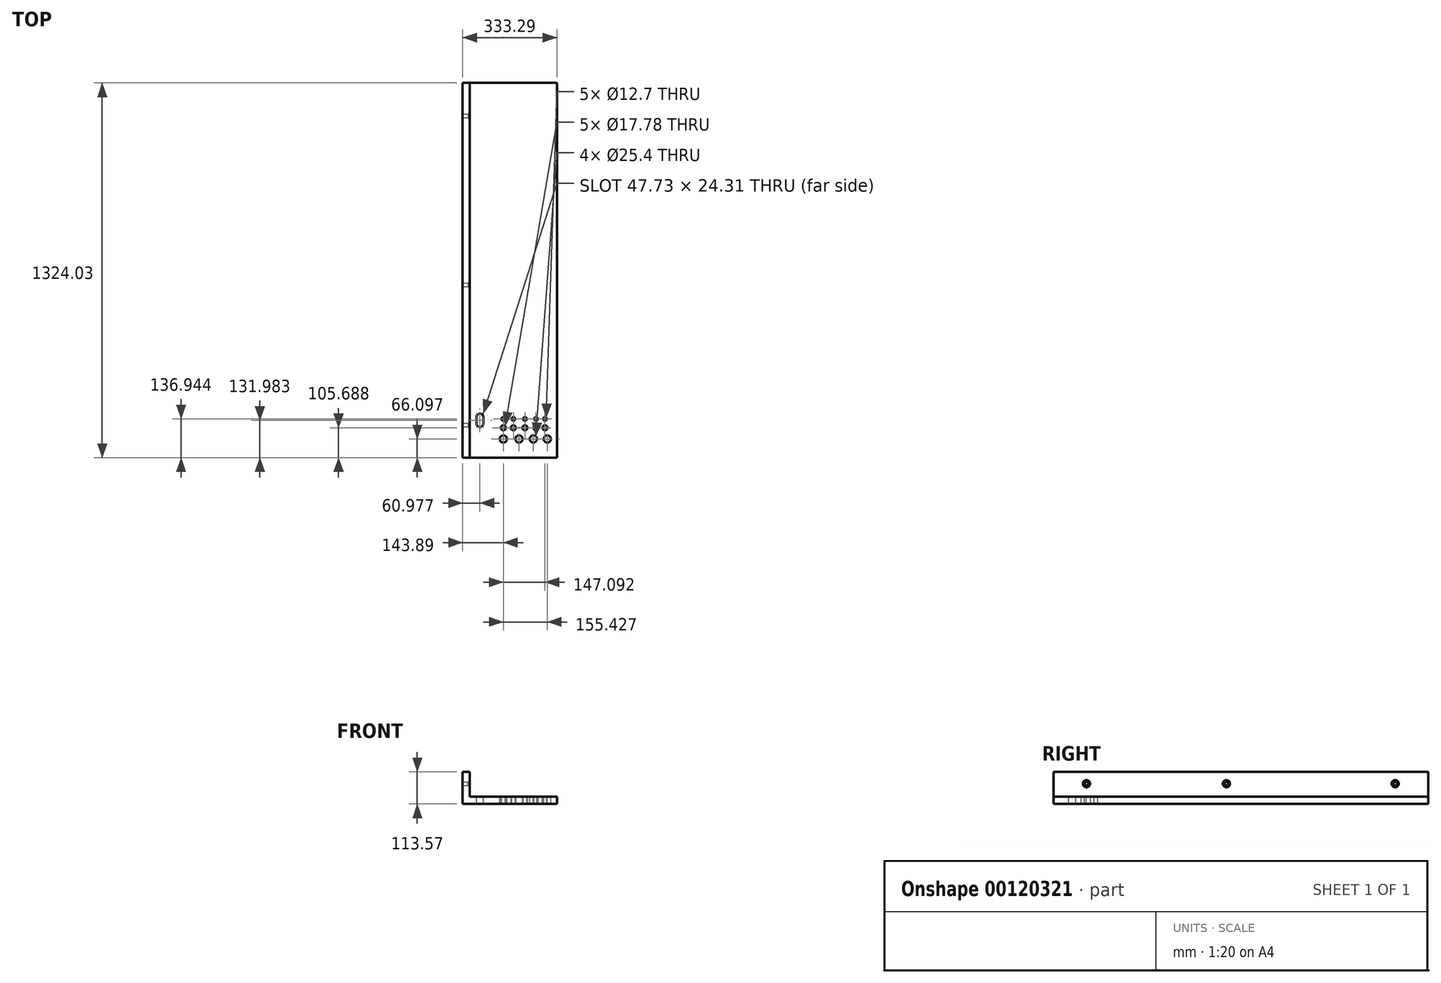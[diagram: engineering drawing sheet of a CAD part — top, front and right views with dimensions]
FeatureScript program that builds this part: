
annotation { "Feature Type Name" : "Feature", "Feature Type Description" : "" }
export const myFeature = defineFeature(function(context is Context, id is Id, definition is map)
    precondition{}
    {
        {
            var Q0;
            Q0=qCreatedBy(makeId("Top.planeOp"),FACE);
            var sketch = newSketch(context, id + "F0", { "sketchPlane" : qUnion([Q0])});
            skLineSegment(sketch, "E0.bottom", {"start": v(-154.05, 84.32) * mm, "end": v(153.84, 84.32) * mm});
            skLineSegment(sketch, "E0.top", {"start": v(-154.05, -115.94) * mm, "end": v(153.84, -115.94) * mm});
            skLineSegment(sketch, "E0.left", {"start": v(-154.05, 84.32) * mm, "end": v(-154.05, -115.94) * mm});
            skLineSegment(sketch, "E0.right", {"start": v(153.84, 84.32) * mm, "end": v(153.84, -115.94) * mm});
            skSolve(sketch);
        }
        {
            var Q0;
            Q0=makeQuery(id+"F0.imprint","IMPRINT",FACE,{"disambiguationData":[TD([[makeQuery(id+"F0.imprint","IMPRINT",EDGE,{"derivedFrom":sQuery(id+"F0.wireOp",EDGE,"E0.bottom")}),-1.0]])]});
            extrude(context, id + "F1", {"entities" : qUnion([Q0]), "depth" : 25.4 * mm});
        }
        {
            var Q0;
            Q0=makeQuery(id+"F1.opExtrude","SWEPT_FACE",FACE,{"disambiguationData":[OSD([sQuery(id+"F0.wireOp",EDGE,"E0.bottom")])]});
            var sketch = newSketch(context, id + "F2", { "sketchPlane" : qUnion([Q0])});
            skLineSegment(sketch, "E1.bottom", {"start": v(-153.84, 25.4) * mm, "end": v(154.05, 25.4) * mm});
            skLineSegment(sketch, "E1.top", {"start": v(-153.84, 0) * mm, "end": v(154.05, 0) * mm});
            skLineSegment(sketch, "E1.left", {"start": v(-153.84, 25.4) * mm, "end": v(-153.84, 0) * mm});
            skLineSegment(sketch, "E1.right", {"start": v(154.05, 25.4) * mm, "end": v(154.05, 0) * mm});
            skSolve(sketch);
        }
        {
            var Q0;
            Q0=makeQuery(id+"F2.imprint","IMPRINT",FACE,{"disambiguationData":[TD([[makeQuery(id+"F2.imprint","IMPRINT",EDGE,{"derivedFrom":sQuery(id+"F2.wireOp",EDGE,"E1.bottom")}),1.0]])]});
            extrude(context, id + "F3", {"entities" : qUnion([Q0]), "operationType" : NewBodyOperationType.ADD, "depth" : 174.76 * mm});
        }
        {
            var Q0;
            Q0=makeQuery(id+"F3.opExtrude","CAP_FACE",FACE,{"disambiguationData":[OSD([sQuery(id+"F2.wireOp",EDGE,"E1.bottom"),sQuery(id+"F2.wireOp",EDGE,"E1.top"),sQuery(id+"F2.wireOp",EDGE,"E1.left"),sQuery(id+"F2.wireOp",EDGE,"E1.right")])],"isStart":false});
            extrude(context, id + "F4", {"entities" : qUnion([Q0]), "operationType" : NewBodyOperationType.ADD, "depth" : 949 * mm});
        }
        {
            var Q0;
            {var subQ0=sQuery(id+"F2.wireOp",EDGE,"E1.right");Q0=makeQuery(id+"F4.boolean.opBoolean","MERGE",FACE,{"derivedFrom":[makeQuery(id+"F3.boolean.opBoolean","MERGE",FACE,{"derivedFrom":[makeQuery(id+"F1.opExtrude","SWEPT_FACE",FACE,{"disambiguationData":[OSD([sQuery(id+"F0.wireOp",EDGE,"E0.left")])]}),makeQuery(id+"F3.opExtrude","SWEPT_FACE",FACE,{"disambiguationData":[OSD([subQ0])]})]}),makeQuery(id+"F4.opExtrude","SWEPT_FACE",FACE,{"disambiguationData":[OSD([subQ0])]})]});}
            var sketch = newSketch(context, id + "F5", { "sketchPlane" : qUnion([Q0])});
            skLineSegment(sketch, "E2.bottom", {"start": v(-1208.09, 25.4) * mm, "end": v(115.94, 25.4) * mm});
            skLineSegment(sketch, "E2.top", {"start": v(-1208.09, 0) * mm, "end": v(115.94, 0) * mm});
            skLineSegment(sketch, "E2.left", {"start": v(-1208.09, 25.4) * mm, "end": v(-1208.09, 0) * mm});
            skLineSegment(sketch, "E2.right", {"start": v(115.94, 25.4) * mm, "end": v(115.94, 0) * mm});
            skSolve(sketch);
        }
        {
            var Q0;
            Q0=makeQuery(id+"F5.imprint","IMPRINT",FACE,{"disambiguationData":[TD([[makeQuery(id+"F5.imprint","IMPRINT",EDGE,{"derivedFrom":sQuery(id+"F5.wireOp",EDGE,"E2.bottom")}),-1.0]])]});
            extrude(context, id + "F6", {"entities" : qUnion([Q0]), "operationType" : NewBodyOperationType.ADD, "depth" : 25.4 * mm});
        }
        {
            var Q0;
            {var subQ0=sQuery(id+"F2.wireOp",EDGE,"E1.bottom");Q0=makeQuery(id+"F6.boolean.opBoolean","MERGE",FACE,{"derivedFrom":[makeQuery(id+"F4.boolean.opBoolean","MERGE",FACE,{"derivedFrom":[makeQuery(id+"F3.boolean.opBoolean","MERGE",FACE,{"derivedFrom":[makeQuery(id+"F1.opExtrude","CAP_FACE",FACE,{"disambiguationData":[OSD([sQuery(id+"F0.wireOp",EDGE,"E0.bottom"),sQuery(id+"F0.wireOp",EDGE,"E0.top"),sQuery(id+"F0.wireOp",EDGE,"E0.left"),sQuery(id+"F0.wireOp",EDGE,"E0.right")])],"isStart":false}),makeQuery(id+"F3.opExtrude","SWEPT_FACE",FACE,{"disambiguationData":[OSD([subQ0])]})]}),makeQuery(id+"F4.opExtrude","SWEPT_FACE",FACE,{"disambiguationData":[OSD([subQ0])]})]}),makeQuery(id+"F6.opExtrude","SWEPT_FACE",FACE,{"disambiguationData":[OSD([sQuery(id+"F5.wireOp",EDGE,"E2.bottom")])]})]});}
            var sketch = newSketch(context, id + "F7", { "sketchPlane" : qUnion([Q0])});
            skLineSegment(sketch, "E3.bottom", {"start": v(-179.45, -115.94) * mm, "end": v(-154.05, -115.94) * mm});
            skLineSegment(sketch, "E3.top", {"start": v(-179.45, 1208.09) * mm, "end": v(-154.05, 1208.09) * mm});
            skLineSegment(sketch, "E3.left", {"start": v(-179.45, -115.94) * mm, "end": v(-179.45, 1208.09) * mm});
            skLineSegment(sketch, "E3.right", {"start": v(-154.05, -115.94) * mm, "end": v(-154.05, 1208.09) * mm});
            skSolve(sketch);
        }
        {
            var Q0;
            Q0=makeQuery(id+"F7.imprint","IMPRINT",FACE,{"disambiguationData":[TD([[makeQuery(id+"F7.imprint","IMPRINT",EDGE,{"derivedFrom":sQuery(id+"F7.wireOp",EDGE,"E3.bottom")}),1.0]])]});
            extrude(context, id + "F8", {"entities" : qUnion([Q0]), "operationType" : NewBodyOperationType.ADD, "depth" : 88.17 * mm});
        }
        {
            var Q0;
            Q0=makeQuery(id+"F8.opExtrude","SWEPT_FACE",FACE,{"disambiguationData":[OSD([sQuery(id+"F7.wireOp",EDGE,"E3.right")])]});
            var sketch = newSketch(context, id + "F9", { "sketchPlane" : qUnion([Q0])});
            skPoint(sketch, "E4", {"position": v(0, 71.74) * mm});
            skPoint(sketch, "E5", {"position": v(1091.25, 71.74) * mm});
            skPoint(sketch, "E6", {"position": v(494.8, 71.74) * mm});
            skSolve(sketch);
        }
        {
            var Q0;
            Q0=sQuery(id+"F9.wireOp",VERTEX,"E4");
            var Q1;
            Q1=sQuery(id+"F9.wireOp",VERTEX,"E6");
            var Q2;
            Q2=sQuery(id+"F9.wireOp",VERTEX,"E5");
            var Q3;
            Q3=makeQuery(id+"F1.opExtrude","SWEPT_BODY",BODY,{"disambiguationData":[OSD([sQuery(id+"F0.wireOp",EDGE,"E0.bottom"),sQuery(id+"F0.wireOp",EDGE,"E0.top"),sQuery(id+"F0.wireOp",EDGE,"E0.left"),sQuery(id+"F0.wireOp",EDGE,"E0.right")])]});
            hole(context, id + "F10", {"style" : HoleStyle.C_SINK, "endStyle" : HoleEndStyle.THROUGH, "holeDiameter" : 12.7 * mm, "cSinkDiameter" : 25.4 * mm, "cSinkAngle" : 90 * degree, "locations" : qUnion([Q0, Q1, Q2]), "scope" : qUnion([Q3]), "isTappedThrough" : true});
        }
        {
            var Q0;
            {var subQ0=sQuery(id+"F2.wireOp",EDGE,"E1.bottom");Q0=makeQuery(id+"F6.boolean.opBoolean","MERGE",FACE,{"derivedFrom":[makeQuery(id+"F4.boolean.opBoolean","MERGE",FACE,{"derivedFrom":[makeQuery(id+"F3.boolean.opBoolean","MERGE",FACE,{"derivedFrom":[makeQuery(id+"F1.opExtrude","CAP_FACE",FACE,{"disambiguationData":[OSD([sQuery(id+"F0.wireOp",EDGE,"E0.bottom"),sQuery(id+"F0.wireOp",EDGE,"E0.top"),sQuery(id+"F0.wireOp",EDGE,"E0.left"),sQuery(id+"F0.wireOp",EDGE,"E0.right")])],"isStart":false}),makeQuery(id+"F3.opExtrude","SWEPT_FACE",FACE,{"disambiguationData":[OSD([subQ0])]})]}),makeQuery(id+"F4.opExtrude","SWEPT_FACE",FACE,{"disambiguationData":[OSD([subQ0])]})]}),makeQuery(id+"F6.opExtrude","SWEPT_FACE",FACE,{"disambiguationData":[OSD([sQuery(id+"F5.wireOp",EDGE,"E2.bottom")])]})]});}
            var sketch = newSketch(context, id + "F11", { "sketchPlane" : qUnion([Q0])});
            skLineSegment(sketch, "E7", {"start": v(-130.63, -43.56) * mm, "end": v(-130.63, -63.37) * mm});
            skLineSegment(sketch, "E8", {"start": v(-130.63, -63.37) * mm, "end": v(-130.63, -43.56) * mm});
            skLineSegment(sketch, "E9", {"start": v(-106.32, -43.56) * mm, "end": v(-106.32, -66.98) * mm});
            skArc(sketch, "E10", {"start": v(-106.32, -43.56) * mm, "mid": v(-118.47, -31.4) * mm, "end": v(-130.63, -43.56) * mm});
            skLineSegment(sketch, "E11", {"start": v(-130.63, -66.98) * mm, "end": v(-130.63, -63.37) * mm});
            skArc(sketch, "E12", {"start": v(-130.63, -66.98) * mm, "mid": v(-118.47, -79.13) * mm, "end": v(-106.32, -66.98) * mm});
            skLineSegment(sketch, "E13", {"start": v(-130.63, 4.33) * mm, "end": v(-130.63, 27.75) * mm});
            skLineSegment(sketch, "E14", {"start": v(-106.32, 4.33) * mm, "end": v(-106.32, 27.75) * mm});
            skArc(sketch, "E15", {"start": v(-106.32, 27.75) * mm, "mid": v(-118.47, 39.9) * mm, "end": v(-130.63, 27.75) * mm});
            skArc(sketch, "E16", {"start": v(-130.63, 4.33) * mm, "mid": v(-118.47, -7.82) * mm, "end": v(-106.32, 4.33) * mm});
            skCircle(sketch, "E17", {"center": v(-35.56, 21) * mm, "radius": 7.41 * mm});
            skCircle(sketch, "E18", {"center": v(-35.56, -10.25) * mm, "radius": 11.38 * mm});
            skCircle(sketch, "E19", {"center": v(-35.56, -49.84) * mm, "radius": 15.67 * mm});
            skCircle(sketch, "E20", {"center": v(0, 21) * mm, "radius": 7.5 * mm});
            skCircle(sketch, "E21", {"center": v(40.69, 21) * mm, "radius": 6.8 * mm});
            skCircle(sketch, "E22", {"center": v(79.76, 21) * mm, "radius": 8.62 * mm});
            skCircle(sketch, "E23", {"center": v(111.53, 21) * mm, "radius": 8.1 * mm});
            skCircle(sketch, "E24", {"center": v(0, -10.25) * mm, "radius": 10.25 * mm});
            skCircle(sketch, "E25", {"center": v(40.69, -10.25) * mm, "radius": 11.38 * mm});
            skCircle(sketch, "E26", {"center": v(79.76, -10.25) * mm, "radius": 11.38 * mm});
            skCircle(sketch, "E27", {"center": v(111.53, -10.25) * mm, "radius": 11.38 * mm});
            skCircle(sketch, "E28", {"center": v(19.85, -49.84) * mm, "radius": 15.67 * mm});
            skCircle(sketch, "E29", {"center": v(70.38, -49.84) * mm, "radius": 15.67 * mm});
            skCircle(sketch, "E30", {"center": v(119.87, -49.84) * mm, "radius": 15.67 * mm});
            skSolve(sketch);
        }
        {
            var Q0;
            Q0=sQuery(id+"F11.wireOp",VERTEX,"E17.center");
            var Q1;
            Q1=sQuery(id+"F11.wireOp",VERTEX,"E20.center");
            var Q2;
            Q2=sQuery(id+"F11.wireOp",VERTEX,"E21.center");
            var Q3;
            Q3=sQuery(id+"F11.wireOp",VERTEX,"E22.center");
            var Q4;
            Q4=sQuery(id+"F11.wireOp",VERTEX,"E23.center");
            var Q5;
            Q5=makeQuery(id+"F1.opExtrude","SWEPT_BODY",BODY,{"disambiguationData":[OSD([sQuery(id+"F0.wireOp",EDGE,"E0.bottom"),sQuery(id+"F0.wireOp",EDGE,"E0.top"),sQuery(id+"F0.wireOp",EDGE,"E0.left"),sQuery(id+"F0.wireOp",EDGE,"E0.right")])]});
            hole(context, id + "F12", {"style" : HoleStyle.SIMPLE, "endStyle" : HoleEndStyle.THROUGH, "holeDiameter" : 12.7 * mm, "locations" : qUnion([Q0, Q1, Q2, Q3, Q4]), "scope" : qUnion([Q5]), "isTappedThrough" : true});
        }
        {
            var Q0;
            Q0=sQuery(id+"F11.wireOp",VERTEX,"E18.center");
            var Q1;
            Q1=sQuery(id+"F11.wireOp",VERTEX,"E24.center");
            var Q2;
            Q2=sQuery(id+"F11.wireOp",VERTEX,"E25.center");
            var Q3;
            Q3=sQuery(id+"F11.wireOp",VERTEX,"E26.center");
            var Q4;
            Q4=sQuery(id+"F11.wireOp",VERTEX,"E27.center");
            var Q5;
            Q5=makeQuery(id+"F1.opExtrude","SWEPT_BODY",BODY,{"disambiguationData":[OSD([sQuery(id+"F0.wireOp",EDGE,"E0.bottom"),sQuery(id+"F0.wireOp",EDGE,"E0.top"),sQuery(id+"F0.wireOp",EDGE,"E0.left"),sQuery(id+"F0.wireOp",EDGE,"E0.right")])]});
            hole(context, id + "F13", {"style" : HoleStyle.SIMPLE, "endStyle" : HoleEndStyle.THROUGH, "holeDiameter" : 17.78 * mm, "locations" : qUnion([Q0, Q1, Q2, Q3, Q4]), "scope" : qUnion([Q5]), "isTappedThrough" : true});
        }
        {
            var Q0;
            Q0=sQuery(id+"F11.wireOp",VERTEX,"E19.center");
            var Q1;
            Q1=sQuery(id+"F11.wireOp",VERTEX,"E28.center");
            var Q2;
            Q2=sQuery(id+"F11.wireOp",VERTEX,"E29.center");
            var Q3;
            Q3=sQuery(id+"F11.wireOp",VERTEX,"E30.center");
            var Q4;
            Q4=makeQuery(id+"F1.opExtrude","SWEPT_BODY",BODY,{"disambiguationData":[OSD([sQuery(id+"F0.wireOp",EDGE,"E0.bottom"),sQuery(id+"F0.wireOp",EDGE,"E0.top"),sQuery(id+"F0.wireOp",EDGE,"E0.left"),sQuery(id+"F0.wireOp",EDGE,"E0.right")])]});
            hole(context, id + "F14", {"style" : HoleStyle.SIMPLE, "endStyle" : HoleEndStyle.THROUGH, "holeDiameter" : 25.4 * mm, "locations" : qUnion([Q0, Q1, Q2, Q3]), "scope" : qUnion([Q4]), "isTappedThrough" : true});
        }
        {
            var Q0;
            Q0=makeQuery(id+"F11.imprint","IMPRINT",FACE,{"disambiguationData":[TD([[makeQuery(id+"F11.imprint","IMPRINT",EDGE,{"derivedFrom":sQuery(id+"F11.wireOp",EDGE,"E13")}),-1.0]])]});
            var Q1;
            Q1=makeQuery(id+"F11.imprint","IMPRINT",FACE,{"disambiguationData":[TD([[makeQuery(id+"F11.imprint","IMPRINT",EDGE,{"derivedFrom":sQuery(id+"F11.wireOp",EDGE,"E8")}),-1.0]])]});
            extrude(context, id + "F15", {"entities" : qUnion([Q0, Q1]), "operationType" : NewBodyOperationType.REMOVE, "oppositeDirection" : true, "depth" : 25.4 * mm});
        }
    });
